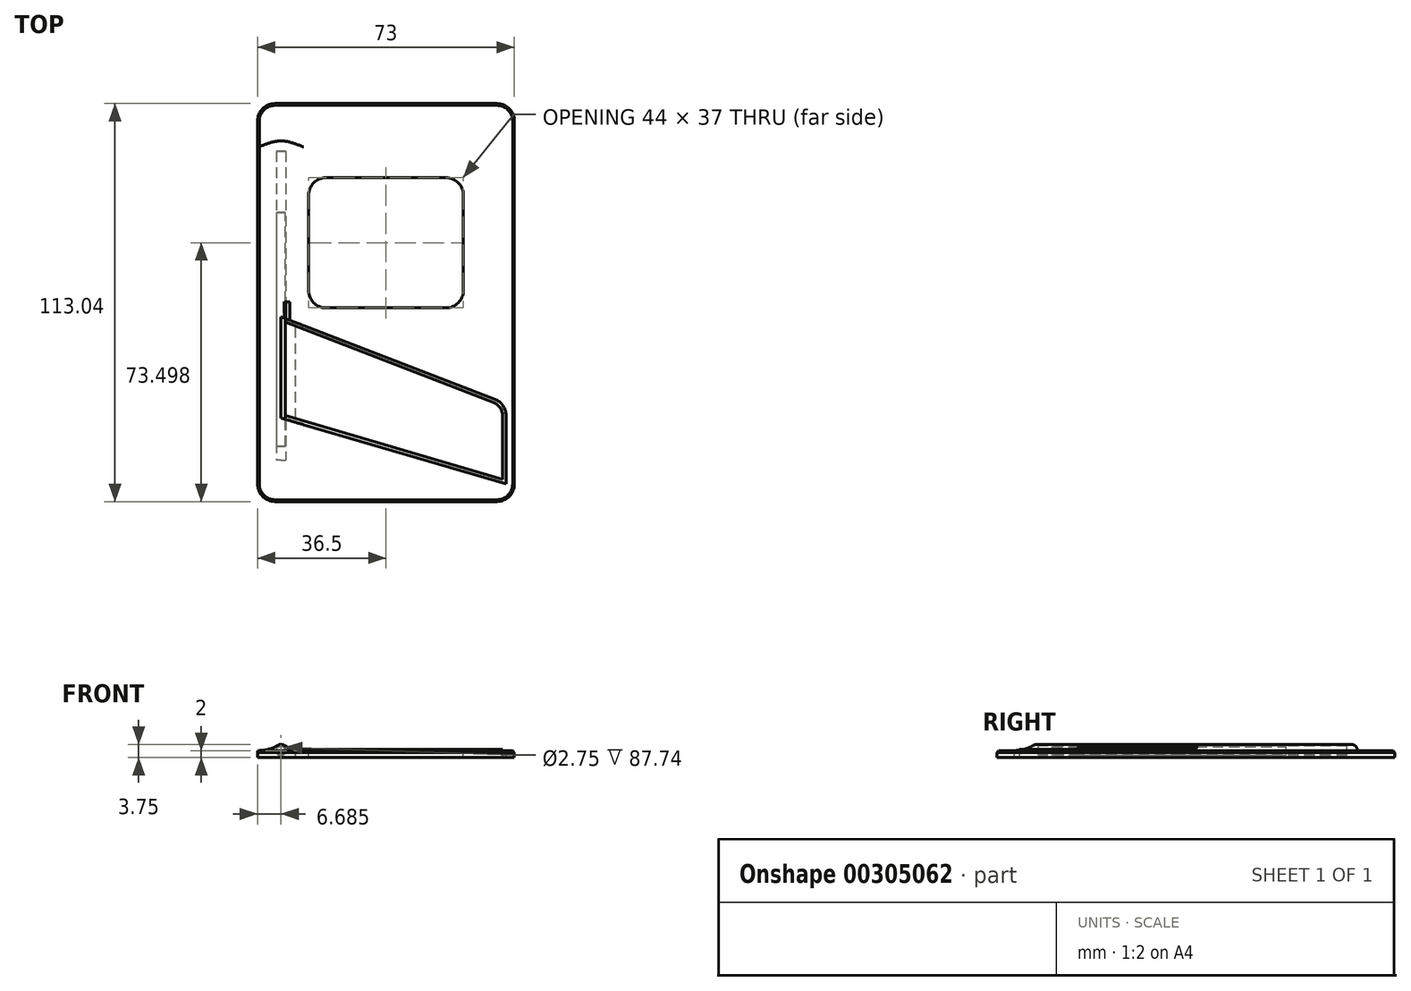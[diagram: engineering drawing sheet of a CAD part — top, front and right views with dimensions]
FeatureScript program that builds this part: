
annotation { "Feature Type Name" : "Feature", "Feature Type Description" : "" }
export const myFeature = defineFeature(function(context is Context, id is Id, definition is map)
    precondition{}
    {
        {
            var Q0;
            Q0=qCreatedBy(makeId("Top.planeOp"),FACE);
            var sketch = newSketch(context, id + "F0", { "sketchPlane" : qUnion([Q0])});
            skLineSegment(sketch, "E0.0.0", {"start": v(31.5, 56.52) * mm, "end": v(-31.5, 56.52) * mm});
            skArc(sketch, "E0.0.1", {"start": v(-31.5, 56.52) * mm, "mid": v(-35.04, 55.06) * mm, "end": v(-36.5, 51.52) * mm});
            skLineSegment(sketch, "E0.0.2", {"start": v(-36.5, 51.52) * mm, "end": v(-36.5, -51.52) * mm});
            skArc(sketch, "E0.0.3", {"start": v(-36.5, -51.52) * mm, "mid": v(-35.04, -55.06) * mm, "end": v(-31.5, -56.52) * mm});
            skLineSegment(sketch, "E0.0.4", {"start": v(-31.5, -56.52) * mm, "end": v(31.5, -56.52) * mm});
            skArc(sketch, "E0.0.5", {"start": v(31.5, -56.52) * mm, "mid": v(35.04, -55.06) * mm, "end": v(36.5, -51.52) * mm});
            skLineSegment(sketch, "E0.0.6", {"start": v(36.5, -51.52) * mm, "end": v(36.5, 51.52) * mm});
            skArc(sketch, "E0.0.7", {"start": v(36.5, 51.52) * mm, "mid": v(35.04, 55.06) * mm, "end": v(31.5, 56.52) * mm});
            skLineSegment(sketch, "E1", {"start": v(-31.5, 51.52) * mm, "end": v(31.5, -51.52) * mm, "construction": true});
            skSolve(sketch);
        }
        {
            var Q0;
            Q0=makeQuery(id+"F0.imprint","IMPRINT",FACE,{"disambiguationData":[TD([[makeQuery(id+"F0.imprint","IMPRINT",EDGE,{"derivedFrom":sQuery(id+"F0.wireOp",EDGE,"E0.0.0")}),1.0]])]});
            extrude(context, id + "F1", {"entities" : qUnion([Q0]), "depth" : 2 * mm});
        }
        {
            var Q0;
            Q0=qCreatedBy(makeId("Front.planeOp"),FACE);
            var sketch = newSketch(context, id + "F2", { "sketchPlane" : qUnion([Q0])});
            skCircle(sketch, "E2", {"center": v(-29.81, 2) * mm, "radius": 1.75 * mm});
            skSolve(sketch);
        }
        {
            var Q0;
            Q0 = qSketchRegion(id + "F2", true);
            extrude(context, id + "F3", {"entities" : qUnion([Q0]), "operationType" : NewBodyOperationType.ADD, "oppositeDirection" : true, "depth" : 45.9 * mm, "hasSecondDirection" : true, "secondDirectionOppositeDirection" : false, "secondDirectionDepth" : 45.2 * mm});
        }
        {
            var Q0;
            Q0=makeQuery(id+"F3.boolean.opBoolean","INTERSECT",EDGE,{"disambiguationData":[OD(1.0)],"derivedFrom":[makeQuery(id+"F1.opExtrude","CAP_FACE",FACE,{"disambiguationData":[OSD([sQuery(id+"F0.wireOp",EDGE,"E0.0.0"),sQuery(id+"F0.wireOp",EDGE,"E0.0.1"),sQuery(id+"F0.wireOp",EDGE,"E0.0.2"),sQuery(id+"F0.wireOp",EDGE,"E0.0.3"),sQuery(id+"F0.wireOp",EDGE,"E0.0.4"),sQuery(id+"F0.wireOp",EDGE,"E0.0.5"),sQuery(id+"F0.wireOp",EDGE,"E0.0.6"),sQuery(id+"F0.wireOp",EDGE,"E0.0.7")])],"isStart":false}),makeQuery(id+"F3.opExtrude","SWEPT_FACE",FACE,{"disambiguationData":[OSD([sQuery(id+"F2.wireOp",EDGE,"E2")])]})]});
            var Q1;
            Q1=makeQuery(id+"F3.boolean.opBoolean","INTERSECT",EDGE,{"disambiguationData":[OD(0.0)],"derivedFrom":[makeQuery(id+"F1.opExtrude","CAP_FACE",FACE,{"disambiguationData":[OSD([sQuery(id+"F0.wireOp",EDGE,"E0.0.0"),sQuery(id+"F0.wireOp",EDGE,"E0.0.1"),sQuery(id+"F0.wireOp",EDGE,"E0.0.2"),sQuery(id+"F0.wireOp",EDGE,"E0.0.3"),sQuery(id+"F0.wireOp",EDGE,"E0.0.4"),sQuery(id+"F0.wireOp",EDGE,"E0.0.5"),sQuery(id+"F0.wireOp",EDGE,"E0.0.6"),sQuery(id+"F0.wireOp",EDGE,"E0.0.7")])],"isStart":false}),makeQuery(id+"F3.opExtrude","SWEPT_FACE",FACE,{"disambiguationData":[OSD([sQuery(id+"F2.wireOp",EDGE,"E2")])]})]});
            fillet(context, id + "F4", {"entities" : qUnion([Q0, Q1]), "radius" : 11 * mm, "tangentPropagation" : true, "allowEdgeOverflow" : false});
        }
        {
            var Q0;
            Q0=makeQuery(id+"F3.opExtrude","CAP_EDGE",EDGE,{"disambiguationData":[OSD([sQuery(id+"F2.wireOp",EDGE,"E2")])],"isStart":false});
            fillet(context, id + "F5", {"entities" : qUnion([Q0]), "radius" : 1.7 * mm, "tangentPropagation" : true, "allowEdgeOverflow" : false});
        }
        {
            var Q0;
            Q0=makeQuery(id+"F1.opExtrude","CAP_FACE",FACE,{"disambiguationData":[OSD([sQuery(id+"F0.wireOp",EDGE,"E0.0.0"),sQuery(id+"F0.wireOp",EDGE,"E0.0.1"),sQuery(id+"F0.wireOp",EDGE,"E0.0.2"),sQuery(id+"F0.wireOp",EDGE,"E0.0.3"),sQuery(id+"F0.wireOp",EDGE,"E0.0.4"),sQuery(id+"F0.wireOp",EDGE,"E0.0.5"),sQuery(id+"F0.wireOp",EDGE,"E0.0.6"),sQuery(id+"F0.wireOp",EDGE,"E0.0.7")])],"isStart":false});
            var sketch = newSketch(context, id + "F6", { "sketchPlane" : qUnion([Q0])});
            skLineSegment(sketch, "E3.bottom", {"start": v(17, 35.48) * mm, "end": v(-17, 35.48) * mm});
            skLineSegment(sketch, "E3.top", {"start": v(17, -1.52) * mm, "end": v(-17, -1.52) * mm});
            skLineSegment(sketch, "E3.left", {"start": v(22, 30.48) * mm, "end": v(22, 3.48) * mm});
            skLineSegment(sketch, "E3.right", {"start": v(-22, 30.48) * mm, "end": v(-22, 3.48) * mm});
            skPoint(sketch, "E3.middle", {"position": v(0, 16.98) * mm});
            skPoint(sketch, "E4.visualSharp", {"position": v(-22, 35.48) * mm});
            skArc(sketch, "E4.filletArc", {"start": v(-17, 35.48) * mm, "mid": v(-20.54, 34.01) * mm, "end": v(-22, 30.48) * mm});
            skPoint(sketch, "E5.visualSharp", {"position": v(22, 35.48) * mm});
            skArc(sketch, "E5.filletArc", {"start": v(22, 30.48) * mm, "mid": v(20.54, 34.01) * mm, "end": v(17, 35.48) * mm});
            skPoint(sketch, "E6.visualSharp", {"position": v(22, -1.52) * mm});
            skArc(sketch, "E6.filletArc", {"start": v(17, -1.52) * mm, "mid": v(20.54, -0.06) * mm, "end": v(22, 3.48) * mm});
            skPoint(sketch, "E7.visualSharp", {"position": v(-22, -1.52) * mm});
            skArc(sketch, "E7.filletArc", {"start": v(-22, 3.48) * mm, "mid": v(-20.54, -0.06) * mm, "end": v(-17, -1.52) * mm});
            skSolve(sketch);
        }
        {
            var Q0;
            Q0=makeQuery(id+"F6.imprint","IMPRINT",FACE,{"disambiguationData":[TD([[makeQuery(id+"F6.imprint","IMPRINT",EDGE,{"derivedFrom":sQuery(id+"F6.wireOp",EDGE,"E3.bottom")}),1.0]])]});
            extrude(context, id + "F7", {"entities" : qUnion([Q0]), "operationType" : NewBodyOperationType.REMOVE, "oppositeDirection" : true, "depth" : 25 * mm});
        }
        {
            var Q0;
            Q0=makeQuery(id+"F1.opExtrude","CAP_FACE",FACE,{"disambiguationData":[OSD([sQuery(id+"F0.wireOp",EDGE,"E0.0.0"),sQuery(id+"F0.wireOp",EDGE,"E0.0.1"),sQuery(id+"F0.wireOp",EDGE,"E0.0.2"),sQuery(id+"F0.wireOp",EDGE,"E0.0.3"),sQuery(id+"F0.wireOp",EDGE,"E0.0.4"),sQuery(id+"F0.wireOp",EDGE,"E0.0.5"),sQuery(id+"F0.wireOp",EDGE,"E0.0.6"),sQuery(id+"F0.wireOp",EDGE,"E0.0.7")])],"isStart":false});
            var sketch = newSketch(context, id + "F8", { "sketchPlane" : qUnion([Q0])});
            skLineSegment(sketch, "E8", {"start": v(-29.81, -32.8) * mm, "end": v(34.12, -51.52) * mm});
            skLineSegment(sketch, "E9", {"start": v(34.12, -51.52) * mm, "end": v(34.12, -28.68) * mm});
            skLineSegment(sketch, "E10", {"start": v(34.12, -28.68) * mm, "end": v(-29.81, -4.06) * mm});
            skLineSegment(sketch, "E11", {"start": v(-29.81, -4.06) * mm, "end": v(-29.81, -32.8) * mm});
            skSolve(sketch);
        }
        {
            var Q0;
            Q0 = qSketchRegion(id + "F8", true);
            extrude(context, id + "F9", {"entities" : qUnion([Q0]), "operationType" : NewBodyOperationType.REMOVE, "oppositeDirection" : true, "depth" : 2 * mm, "hasSecondDirection" : true, "secondDirectionOppositeDirection" : false, "secondDirectionDepth" : 14.3 * mm});
        }
        {
            var Q0;
            Q0=makeQuery(id+"F9.boolean.opBoolean","COPY",EDGE,{"derivedFrom":makeQuery(id+"F9.opExtrude","SWEPT_EDGE",EDGE,{"disambiguationData":[OSD([sQuery(id+"F8.wireOp",EDGE,"E9"),sQuery(id+"F8.wireOp",EDGE,"E10")])]})});
            fillet(context, id + "F10", {"entities" : qUnion([Q0]), "radius" : 5 * mm, "tangentPropagation" : true, "allowEdgeOverflow" : false});
        }
        {
            var Q0;
            Q0=qCreatedBy(makeId("Front.planeOp"),FACE);
            var sketch = newSketch(context, id + "F11", { "sketchPlane" : qUnion([Q0])});
            skCircle(sketch, "E12", {"center": v(-29.81, 2) * mm, "radius": 1.38 * mm});
            skSolve(sketch);
        }
        {
            var Q0;
            Q0 = qSketchRegion(id + "F11", true);
            extrude(context, id + "F12", {"entities" : qUnion([Q0]), "operationType" : NewBodyOperationType.REMOVE, "oppositeDirection" : true, "depth" : 43 * mm, "hasSecondDirection" : true, "secondDirectionOppositeDirection" : false, "secondDirectionDepth" : 32.7 * mm});
        }
        {
            var Q0;
            Q0=makeQuery(id+"F3.opExtrude","CAP_FACE",FACE,{"disambiguationData":[OSD([sQuery(id+"F2.wireOp",EDGE,"E2")])],"isStart":true});
            var sketch = newSketch(context, id + "F13", { "sketchPlane" : qUnion([Q0])});
            skLineSegment(sketch, "E13.0", {"start": v(-30.7, 3.5) * mm, "end": v(-30.7, 3.5) * mm});
            skArc(sketch, "E13.1", {"start": v(-30.7, 3.5) * mm, "mid": v(-33.38, 2.38) * mm, "end": v(-36.26, 2) * mm});
            skLineSegment(sketch, "E14", {"start": v(-36.26, 2) * mm, "end": v(-29.81, 2) * mm});
            skArc(sketch, "E15.0", {"start": v(-29.81, 3.75) * mm, "mid": v(-30.27, 3.69) * mm, "end": v(-30.7, 3.5) * mm});
            skLineSegment(sketch, "E16", {"start": v(-29.81, 2) * mm, "end": v(-29.81, 3.75) * mm});
            skPoint(sketch, "E17.orphan", {"position": v(-28.93, 3.5) * mm});
            skSolve(sketch);
        }
        {
            var Q0;
            Q0 = qSketchRegion(id + "F13", true);
            var Q1;
            Q1=sQuery(id+"F13.wireOp",EDGE,"E16");
            revolve(context, id + "F14", {"operationType" : NewBodyOperationType.ADD, "entities" : qUnion([Q0]), "axis" : qUnion([Q1]), "revolveType" : RevolveType.ONE_DIRECTION, "angle" : 200 * degree});
        }
        {
            var Q0;
            Q0=makeQuery(id+"F12.boolean.opBoolean","COPY",FACE,{"derivedFrom":makeQuery(id+"F12.opExtrude","CAP_FACE",FACE,{"disambiguationData":[OSD([sQuery(id+"F11.wireOp",EDGE,"E12")])],"isStart":true})});
            var sketch = newSketch(context, id + "F15", { "sketchPlane" : qUnion([Q0])});
            skArc(sketch, "E18", {"start": v(28.57, 2.03) * mm, "mid": v(30.83, 1.28) * mm, "end": v(29.37, 3.16) * mm});
            skLineSegment(sketch, "E19", {"start": v(29.37, 3.16) * mm, "end": v(-1.47, 20.85) * mm});
            skLineSegment(sketch, "E20", {"start": v(-1.47, 20.85) * mm, "end": v(-2.16, 19.65) * mm});
            skLineSegment(sketch, "E21", {"start": v(-2.16, 19.65) * mm, "end": v(28.57, 2.03) * mm});
            skSolve(sketch);
        }
        {
            var Q0;
            Q0 = qSketchRegion(id + "F15", true);
            extrude(context, id + "F16", {"entities" : qUnion([Q0]), "operationType" : NewBodyOperationType.REMOVE, "depth" : 32.9 * mm});
        }
        {
            var Q0;
            Q0=makeQuery(id+"F1.opExtrude","CAP_EDGE",EDGE,{"disambiguationData":[OSD([sQuery(id+"F0.wireOp",EDGE,"E0.0.6")])],"isStart":false});
            chamfer(context, id + "F17", {"entities" : qUnion([Q0]), "width" : 0.5 * mm, "tangentPropagation" : true});
        }
        {
            var Q0;
            Q0=qCreatedBy(makeId("Front.planeOp"),FACE);
            var sketch = newSketch(context, id + "F18", { "sketchPlane" : qUnion([Q0])});
            skCircle(sketch, "E22", {"center": v(-29.81, 1.9) * mm, "radius": 1.25 * mm});
            skSolve(sketch);
        }
        {
            var Q0;
            Q0 = qSketchRegion(id + "F18", true);
            extrude(context, id + "F19", {"entities" : qUnion([Q0]), "operationType" : NewBodyOperationType.ADD, "depth" : 32.3 * mm, "hasSecondDirection" : true, "secondDirectionOppositeDirection" : true, "secondDirectionDepth" : 25.6 * mm});
        }
        {
            var Q0;
            Q0=qCreatedBy(makeId("Top.planeOp"),FACE);
            cPlane(context, id + "F20", {"entities" : qUnion([Q0]), "cplaneType" : CPlaneType.OFFSET, "offset" : 1.85 * mm, "width" : 150 * mm, "height" : 150 * mm});
        }
        {
            var Q0;
            Q0=qCreatedBy(id+"F20.planeOp",FACE);
            var sketch = newSketch(context, id + "F21", { "sketchPlane" : qUnion([Q0])});
            skLineSegment(sketch, "E23.0", {"start": v(-29.75, -5.16) * mm, "end": v(-27.97, -5.85) * mm});
            skLineSegment(sketch, "E23.1", {"start": v(-27.97, -5.85) * mm, "end": v(-25.64, -6.74) * mm});
            skLineSegment(sketch, "E23.2", {"start": v(-29.53, -31.84) * mm, "end": v(33.12, -50.19) * mm});
            skLineSegment(sketch, "E23.3", {"start": v(33.12, -50.19) * mm, "end": v(33.12, -32.11) * mm});
            skArc(sketch, "E23.4", {"start": v(30.55, -28.38) * mm, "mid": v(32.41, -29.85) * mm, "end": v(33.12, -32.11) * mm});
            skLineSegment(sketch, "E23.5", {"start": v(30.55, -28.38) * mm, "end": v(-25.64, -6.74) * mm});
            skLineSegment(sketch, "E24", {"start": v(-29.75, -5.16) * mm, "end": v(-29.53, -31.84) * mm});
            skSolve(sketch);
        }
        {
            var Q0;
            Q0 = qSketchRegion(id + "F21", true);
            extrude(context, id + "F22", {"entities" : qUnion([Q0]), "operationType" : NewBodyOperationType.ADD, "endBound" : BoundingType.SYMMETRIC, "depth" : 1 * mm});
        }
        {
            var Q0;
            Q0=makeQuery(id+"F22.opExtrude","CAP_FACE",FACE,{"disambiguationData":[OSD([sQuery(id+"F21.wireOp",EDGE,"E23.0"),sQuery(id+"F21.wireOp",EDGE,"E23.1"),sQuery(id+"F21.wireOp",EDGE,"E23.2"),sQuery(id+"F21.wireOp",EDGE,"E23.3"),sQuery(id+"F21.wireOp",EDGE,"E23.4"),sQuery(id+"F21.wireOp",EDGE,"E23.5"),sQuery(id+"F21.wireOp",EDGE,"E24")])],"isStart":true});
            var sketch = newSketch(context, id + "F23", { "sketchPlane" : qUnion([Q0])});
            skLineSegment(sketch, "E25.0", {"start": v(-25.66, 32.98) * mm, "end": v(33.12, 50.19) * mm});
            skLineSegment(sketch, "E25.1", {"start": v(33.12, 50.19) * mm, "end": v(33.12, 32.11) * mm});
            skArc(sketch, "E25.2", {"start": v(30.55, 28.38) * mm, "mid": v(32.41, 29.85) * mm, "end": v(33.12, 32.11) * mm});
            skLineSegment(sketch, "E25.3", {"start": v(30.55, 28.38) * mm, "end": v(-25.66, 6.74) * mm});
            skLineSegment(sketch, "E26", {"start": v(-25.66, 32.98) * mm, "end": v(-25.66, 6.74) * mm});
            skPoint(sketch, "E27.orphan", {"position": v(-28.7, 32.09) * mm});
            skPoint(sketch, "E28.orphan", {"position": v(-28.7, 5.57) * mm});
            skSolve(sketch);
        }
        {
            var Q0;
            Q0 = qSketchRegion(id + "F23", true);
            var Q1;
            Q1=makeQuery(id+"F1.opExtrude","CAP_FACE",FACE,{"disambiguationData":[OSD([sQuery(id+"F0.wireOp",EDGE,"E0.0.0"),sQuery(id+"F0.wireOp",EDGE,"E0.0.1"),sQuery(id+"F0.wireOp",EDGE,"E0.0.2"),sQuery(id+"F0.wireOp",EDGE,"E0.0.3"),sQuery(id+"F0.wireOp",EDGE,"E0.0.4"),sQuery(id+"F0.wireOp",EDGE,"E0.0.5"),sQuery(id+"F0.wireOp",EDGE,"E0.0.6"),sQuery(id+"F0.wireOp",EDGE,"E0.0.7")])],"isStart":true});
            extrude(context, id + "F24", {"entities" : qUnion([Q0]), "operationType" : NewBodyOperationType.ADD, "endBound" : BoundingType.UP_TO_SURFACE, "endBoundEntityFace" : qUnion([Q1]), "depth" : 25 * mm});
        }
        {
            var Q0;
            Q0=makeQuery(id+"F12.boolean.opBoolean","COPY",FACE,{"derivedFrom":makeQuery(id+"F12.opExtrude","CAP_FACE",FACE,{"disambiguationData":[OSD([sQuery(id+"F11.wireOp",EDGE,"E12")])],"isStart":true})});
            var sketch = newSketch(context, id + "F25", { "sketchPlane" : qUnion([Q0])});
            skCircle(sketch, "E29", {"center": v(29.81, 2) * mm, "radius": 1.38 * mm});
            skSolve(sketch);
        }
        {
            var Q0;
            Q0 = qSketchRegion(id + "F25", true);
            extrude(context, id + "F26", {"entities" : qUnion([Q0]), "operationType" : NewBodyOperationType.REMOVE, "oppositeDirection" : true, "depth" : 12.04 * mm});
        }
        {
            var Q0;
            Q0=makeQuery(id+"F19.opExtrude","CAP_FACE",FACE,{"disambiguationData":[OSD([sQuery(id+"F18.wireOp",EDGE,"E22")])],"isStart":false});
            var sketch = newSketch(context, id + "F27", { "sketchPlane" : qUnion([Q0])});
            skCircle(sketch, "E30.0", {"center": v(-29.81, 1.9) * mm, "radius": 1.25 * mm});
            skSolve(sketch);
        }
        {
            var Q0;
            Q0 = qSketchRegion(id + "F27", true);
            extrude(context, id + "F28", {"entities" : qUnion([Q0]), "operationType" : NewBodyOperationType.ADD, "depth" : 8.5 * mm});
        }
    });
